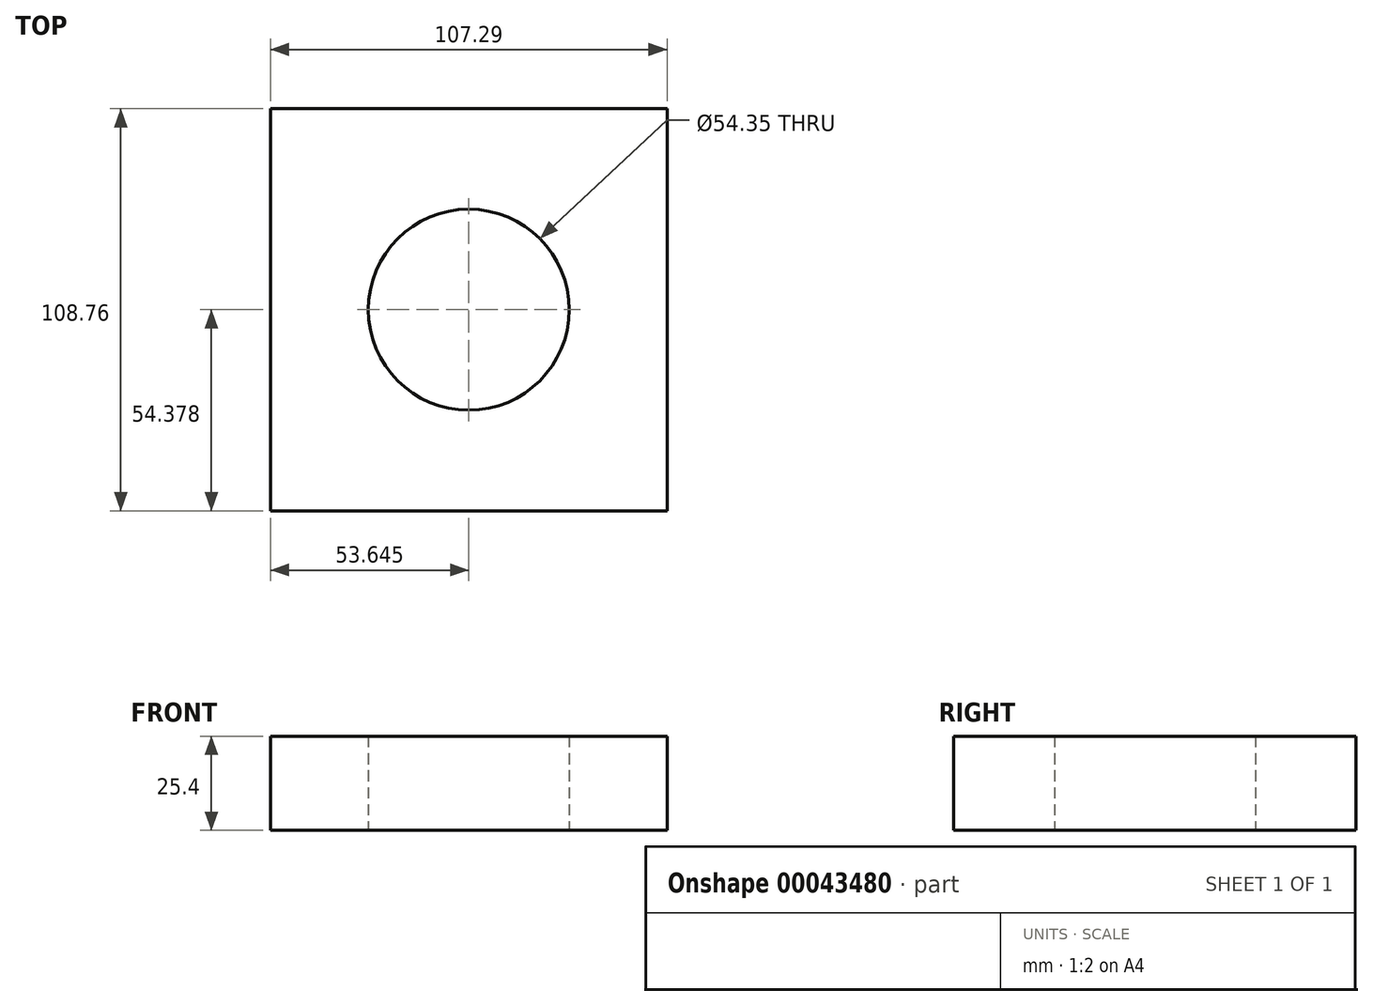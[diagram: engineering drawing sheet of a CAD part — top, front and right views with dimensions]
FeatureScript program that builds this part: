
annotation { "Feature Type Name" : "Feature", "Feature Type Description" : "" }
export const myFeature = defineFeature(function(context is Context, id is Id, definition is map)
    precondition{}
    {
        {
            var Q0;
            Q0=qCreatedBy(makeId("Top.planeOp"),FACE);
            var sketch = newSketch(context, id + "F0", { "sketchPlane" : qUnion([Q0])});
            skLineSegment(sketch, "E0.bottom", {"start": v(0, 0) * mm, "end": v(107.29, 0) * mm});
            skLineSegment(sketch, "E0.top", {"start": v(0, -108.76) * mm, "end": v(107.29, -108.76) * mm});
            skLineSegment(sketch, "E0.left", {"start": v(0, 0) * mm, "end": v(0, -108.76) * mm});
            skLineSegment(sketch, "E0.right", {"start": v(107.29, 0) * mm, "end": v(107.29, -108.76) * mm});
            skLineSegment(sketch, "E1", {"start": v(0, -108.76) * mm, "end": v(107.29, 0) * mm});
            skCircle(sketch, "E2", {"center": v(53.64, -54.38) * mm, "radius": 27.18 * mm});
            skSolve(sketch);
        }
        {
            var Q0;
            {var subQ4=sQuery(id+"F0.wireOp",EDGE,"E0.bottom");Q0=makeQuery(id+"F0.imprint","IMPRINT",FACE,{"disambiguationData":[TD([[makeQuery(id+"F0.imprint","IMPRINT",EDGE,{"derivedFrom":subQ4}),-1.0]])]});}
            var Q1;
            {var subQ0=sQuery(id+"F0.wireOp",EDGE,"E2");var subQ1=sQuery(id+"F0.wireOp",EDGE,"E1");var subQ3=makeQuery(id+"F0.imprint","INTERSECT",VERTEX,{"disambiguationData":[OD(0.0)],"derivedFrom":[subQ1,subQ0]});Q1=makeQuery(id+"F0.imprint","IMPRINT",FACE,{"disambiguationData":[TD([[makeQuery(id+"F0.imprint","IMPRINT",EDGE,{"disambiguationData":[TD([[subQ3,-1.0]])],"derivedFrom":subQ1}),-1.0]])]});}
            extrude(context, id + "F1", {"entities" : qUnion([Q0, Q1]), "depth" : 25.4 * mm});
        }
    });
